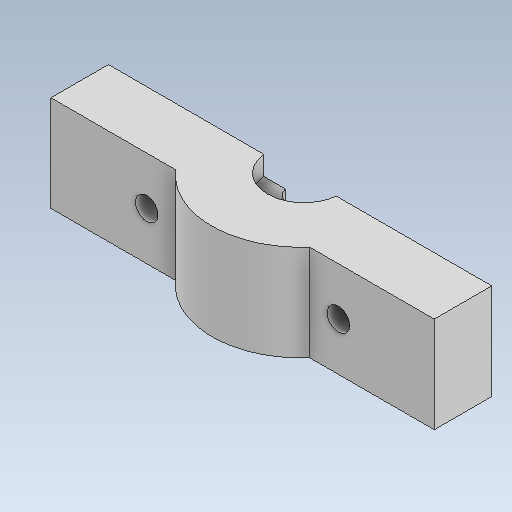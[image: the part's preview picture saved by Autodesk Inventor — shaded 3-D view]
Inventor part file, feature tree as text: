
AUTODESK INVENTOR PART (.ipt)
format: ipt  version: 2020.2 (Build 242310000, 310)  size: 141,312 bytes
history: native  units: mm
features: sketch x5, extrude x4, hole x1
ambient origin geometry x8: Origin, YZ Plane, XZ Plane, XY Plane, X Axis, Y Axis, Z Axis, Center Point
bodies: Solido1 (feature_tree)
feature tree (10):
  extrude  "Estrusione1"  Depth=100.0mm
  extrude  "Estrusione2"  Depth=25.0mm
  extrude  "Estrusione3"  Depth=15.0mm TaperAngle=0.0deg
  hole  "Foro1"  [1 undecoded]
  extrude  "Estrusione4"  TaperAngle=90.0deg  [1 undecoded]
  sketch  "Schizzo1"
  sketch  "Schizzo2"
  sketch  "Schizzo3"
  sketch  "Schizzo4"
  sketch  "Schizzo5"
note: 2 required parameter values undecoded (feature->parameter linkage not recoverable at this tier; creation-order binding heuristic only, values carry confidence <= 0.55)
